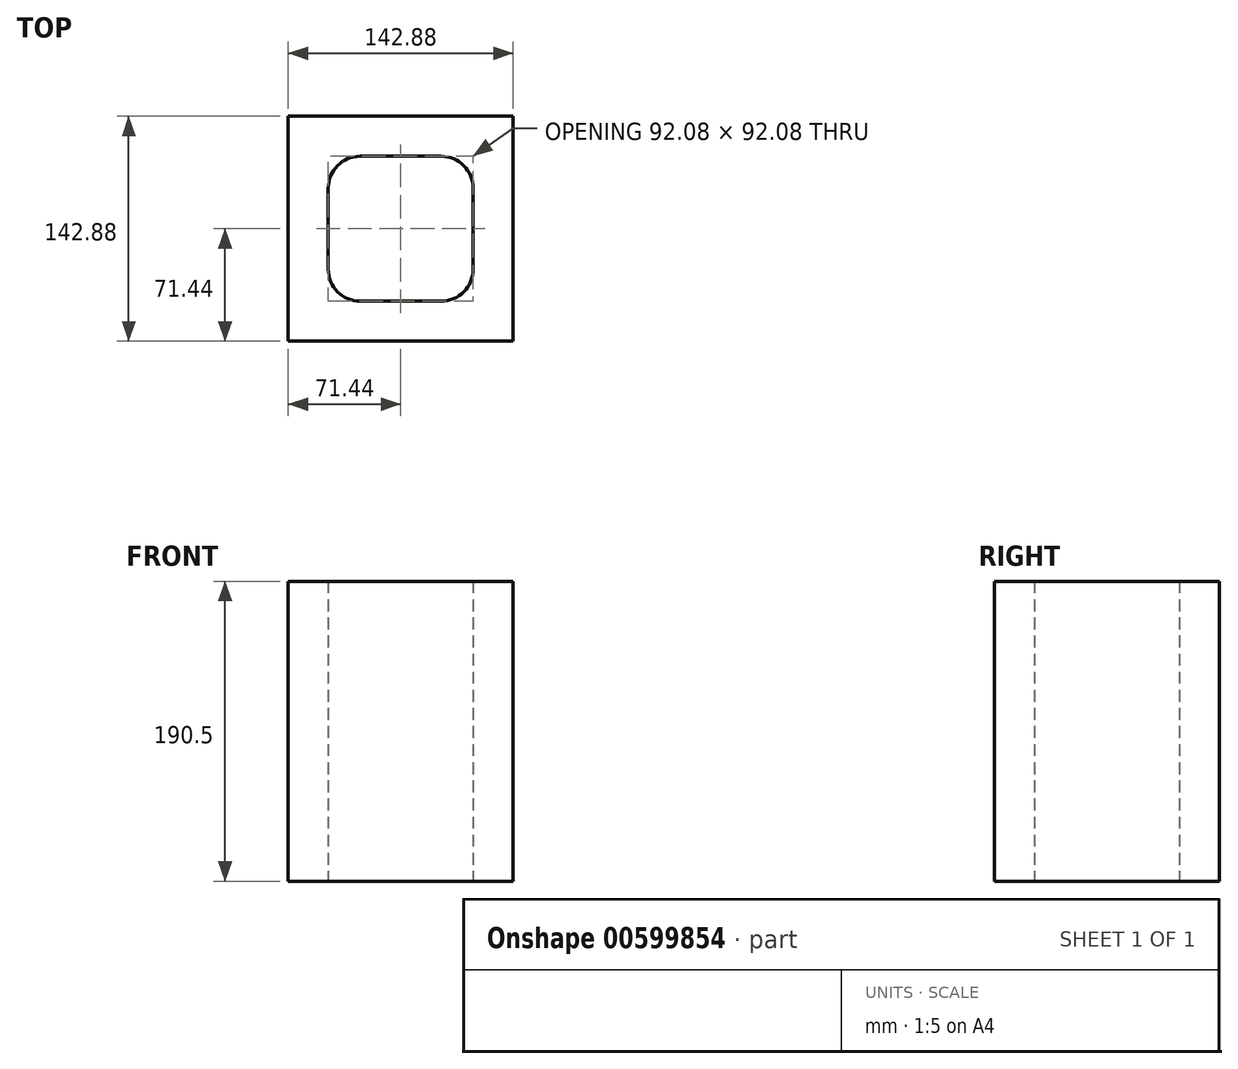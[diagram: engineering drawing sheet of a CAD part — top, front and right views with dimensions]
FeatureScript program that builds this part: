
annotation { "Feature Type Name" : "Feature", "Feature Type Description" : "" }
export const myFeature = defineFeature(function(context is Context, id is Id, definition is map)
    precondition{}
    {
        {
            var Q0;
            Q0=qCreatedBy(makeId("Top.planeOp"),FACE);
            var sketch = newSketch(context, id + "F0", { "sketchPlane" : qUnion([Q0])});
            skLineSegment(sketch, "E0.bottom", {"start": v(71.44, 71.44) * mm, "end": v(-71.44, 71.44) * mm});
            skLineSegment(sketch, "E0.top", {"start": v(71.44, -71.44) * mm, "end": v(-71.44, -71.44) * mm});
            skLineSegment(sketch, "E0.left", {"start": v(71.44, 71.44) * mm, "end": v(71.44, -71.44) * mm});
            skLineSegment(sketch, "E0.right", {"start": v(-71.44, 71.44) * mm, "end": v(-71.44, -71.44) * mm});
            skPoint(sketch, "E0.middle", {"position": v(0, 0) * mm});
            skLineSegment(sketch, "E1.top", {"start": v(25.72, 46.04) * mm, "end": v(-25.72, 46.04) * mm});
            skLineSegment(sketch, "E1.left", {"start": v(46.04, 0) * mm, "end": v(46.04, 25.72) * mm});
            skLineSegment(sketch, "E1.right", {"start": v(-46.04, 0) * mm, "end": v(-46.04, 25.72) * mm});
            skPoint(sketch, "E1.middle", {"position": v(0, 92.08) * mm});
            skLineSegment(sketch, "E2", {"start": v(-132.31, 0) * mm, "end": v(174.12, 0) * mm, "construction": true});
            skPoint(sketch, "E2.endSnap0", {"position": v(71.44, 0) * mm});
            skPoint(sketch, "E3.visualSharp", {"position": v(-46.04, 46.04) * mm});
            skArc(sketch, "E3.filletArc", {"start": v(-25.72, 46.04) * mm, "mid": v(-40.09, 40.09) * mm, "end": v(-46.04, 25.72) * mm});
            skPoint(sketch, "E4.visualSharp", {"position": v(46.04, 46.04) * mm});
            skArc(sketch, "E4.filletArc", {"start": v(46.04, 25.72) * mm, "mid": v(40.09, 40.09) * mm, "end": v(25.72, 46.04) * mm});
            skPoint(sketch, "E5.MirrorP", {"position": v(46.04, -46.04) * mm});
            skArc(sketch, "E6.MirrorCS", {"start": v(46.04, -25.72) * mm, "mid": v(40.09, -40.09) * mm, "end": v(25.72, -46.04) * mm});
            skArc(sketch, "E7.MirrorCS", {"start": v(-25.72, -46.04) * mm, "mid": v(-40.09, -40.09) * mm, "end": v(-46.04, -25.72) * mm});
            skLineSegment(sketch, "E8.MirrorCS", {"start": v(25.72, -46.04) * mm, "end": v(-25.72, -46.04) * mm});
            skLineSegment(sketch, "E9.MirrorCS", {"start": v(46.04, 0) * mm, "end": v(46.04, -25.72) * mm});
            skLineSegment(sketch, "E10.MirrorCS", {"start": v(-46.04, 0) * mm, "end": v(-46.04, -25.72) * mm});
            skPoint(sketch, "E11.MirrorP", {"position": v(-46.04, -46.04) * mm});
            skLineSegment(sketch, "E12", {"start": v(0, 177.27) * mm, "end": v(0, -155.84) * mm, "construction": true});
            skSolve(sketch);
        }
        {
            var Q0;
            Q0=makeQuery(id+"F0.imprint","IMPRINT",FACE,{"disambiguationData":[TD([[makeQuery(id+"F0.imprint","IMPRINT",EDGE,{"derivedFrom":sQuery(id+"F0.wireOp",EDGE,"E0.bottom")}),1.0]])]});
            extrude(context, id + "F1", {"entities" : qUnion([Q0]), "endBound" : BoundingType.SYMMETRIC, "depth" : 190.5 * mm, "offsetDistance" : 25.4 * mm});
        }
    });
